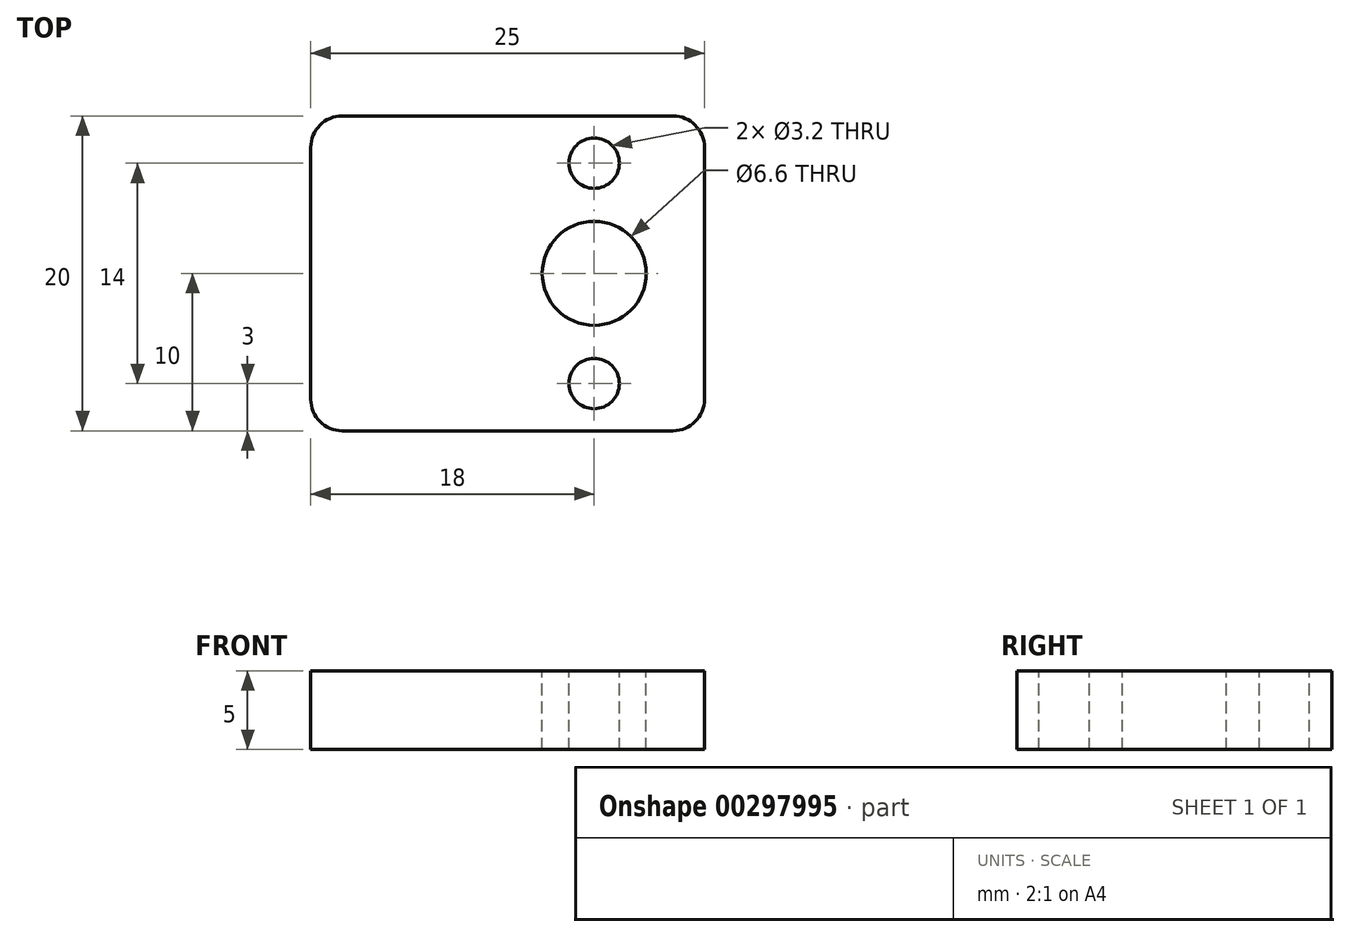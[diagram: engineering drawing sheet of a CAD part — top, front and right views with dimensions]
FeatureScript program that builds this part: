
annotation { "Feature Type Name" : "Feature", "Feature Type Description" : "" }
export const myFeature = defineFeature(function(context is Context, id is Id, definition is map)
    precondition{}
    {
        {
            var Q0;
            Q0=qCreatedBy(makeId("Top.planeOp"),FACE);
            var sketch = newSketch(context, id + "F0", { "sketchPlane" : qUnion([Q0])});
            skLineSegment(sketch, "E0.bottom", {"start": v(12.5, 10) * mm, "end": v(-12.5, 10) * mm});
            skLineSegment(sketch, "E0.top", {"start": v(12.5, -10) * mm, "end": v(-12.5, -10) * mm});
            skLineSegment(sketch, "E0.left", {"start": v(12.5, 10) * mm, "end": v(12.5, -10) * mm});
            skLineSegment(sketch, "E0.right", {"start": v(-12.5, 10) * mm, "end": v(-12.5, -10) * mm});
            skPoint(sketch, "E0.middle", {"position": v(0, 0) * mm});
            skSolve(sketch);
        }
        {
            var Q0;
            Q0=makeQuery(id+"F0.imprint","IMPRINT",FACE,{"disambiguationData":[TD([[makeQuery(id+"F0.imprint","IMPRINT",EDGE,{"derivedFrom":sQuery(id+"F0.wireOp",EDGE,"E0.bottom")}),1.0]])]});
            extrude(context, id + "F1", {"entities" : qUnion([Q0]), "depth" : 5 * mm});
        }
        {
            var Q0;
            Q0=makeQuery(id+"F1.opExtrude","CAP_FACE",FACE,{"disambiguationData":[OSD([sQuery(id+"F0.wireOp",EDGE,"E0.bottom"),sQuery(id+"F0.wireOp",EDGE,"E0.top"),sQuery(id+"F0.wireOp",EDGE,"E0.left"),sQuery(id+"F0.wireOp",EDGE,"E0.right")])],"isStart":false});
            var sketch = newSketch(context, id + "F2", { "sketchPlane" : qUnion([Q0])});
            skLineSegment(sketch, "E1.0", {"start": v(12.5, 10) * mm, "end": v(12.5, -10) * mm});
            skPoint(sketch, "E2", {"position": v(5.5, 0) * mm});
            skSolve(sketch);
        }
        {
            var Q0;
            Q0=sQuery(id+"F2.wireOp",VERTEX,"E2");
            var Q1;
            Q1=makeQuery(id+"F1.opExtrude","SWEPT_BODY",BODY,{"disambiguationData":[OSD([sQuery(id+"F0.wireOp",EDGE,"E0.bottom"),sQuery(id+"F0.wireOp",EDGE,"E0.top"),sQuery(id+"F0.wireOp",EDGE,"E0.left"),sQuery(id+"F0.wireOp",EDGE,"E0.right")])]});
            hole(context, id + "F3", {"style" : HoleStyle.SIMPLE, "endStyle" : HoleEndStyle.BLIND, "standardTappedOrClearance" : lookupTablePath({ "standard" : "ISO", "fit" : "Normal", "size" : "M6", "type" : "Clearance" }), "standardBlindInLast" : lookupTablePath({ "fit" : "Standard", "standard" : "ISO", "size" : "M6", "type" : "Clearance" }), "holeDiameter" : 6.6 * mm, "holeDepth" : 10 * mm, "tappedDepth" : 12 * mm, "tapClearance" : 3, "locations" : qUnion([Q0]), "scope" : qUnion([Q1])});
        }
        {
            var Q0;
            Q0=makeQuery(id+"F1.opExtrude","SWEPT_EDGE",EDGE,{"disambiguationData":[OSD([sQuery(id+"F0.wireOp",EDGE,"E0.top"),sQuery(id+"F0.wireOp",EDGE,"E0.right")])]});
            var Q1;
            Q1=makeQuery(id+"F1.opExtrude","SWEPT_EDGE",EDGE,{"disambiguationData":[OSD([sQuery(id+"F0.wireOp",EDGE,"E0.bottom"),sQuery(id+"F0.wireOp",EDGE,"E0.right")])]});
            var Q2;
            Q2=makeQuery(id+"F1.opExtrude","SWEPT_EDGE",EDGE,{"disambiguationData":[OSD([sQuery(id+"F0.wireOp",EDGE,"E0.top"),sQuery(id+"F0.wireOp",EDGE,"E0.left")])]});
            var Q3;
            Q3=makeQuery(id+"F1.opExtrude","SWEPT_EDGE",EDGE,{"disambiguationData":[OSD([sQuery(id+"F0.wireOp",EDGE,"E0.bottom"),sQuery(id+"F0.wireOp",EDGE,"E0.left")])]});
            fillet(context, id + "F4", {"entities" : qUnion([Q0, Q1, Q2, Q3]), "radius" : 2 * mm, "tangentPropagation" : true, "allowEdgeOverflow" : false});
        }
        {
            var Q0;
            Q0=makeQuery(id+"F1.opExtrude","CAP_FACE",FACE,{"disambiguationData":[OSD([sQuery(id+"F0.wireOp",EDGE,"E0.bottom"),sQuery(id+"F0.wireOp",EDGE,"E0.top"),sQuery(id+"F0.wireOp",EDGE,"E0.left"),sQuery(id+"F0.wireOp",EDGE,"E0.right")])],"isStart":false});
            var sketch = newSketch(context, id + "F5", { "sketchPlane" : qUnion([Q0])});
            skPoint(sketch, "E3", {"position": v(5.5, -7) * mm});
            skPoint(sketch, "E4", {"position": v(5.5, 7) * mm});
            skSolve(sketch);
        }
        {
            var Q0;
            Q0=sQuery(id+"F5.wireOp",VERTEX,"E4");
            var Q1;
            Q1=sQuery(id+"F5.wireOp",VERTEX,"E3");
            var Q2;
            Q2=makeQuery(id+"F1.opExtrude","SWEPT_BODY",BODY,{"disambiguationData":[OSD([sQuery(id+"F0.wireOp",EDGE,"E0.bottom"),sQuery(id+"F0.wireOp",EDGE,"E0.top"),sQuery(id+"F0.wireOp",EDGE,"E0.left"),sQuery(id+"F0.wireOp",EDGE,"E0.right")])]});
            hole(context, id + "F6", {"style" : HoleStyle.SIMPLE, "endStyle" : HoleEndStyle.BLIND, "holeDiameter" : 3.2 * mm, "holeDepth" : 6 * mm, "tappedDepth" : 12 * mm, "tapClearance" : 3, "locations" : qUnion([Q0, Q1]), "scope" : qUnion([Q2])});
        }
    });
